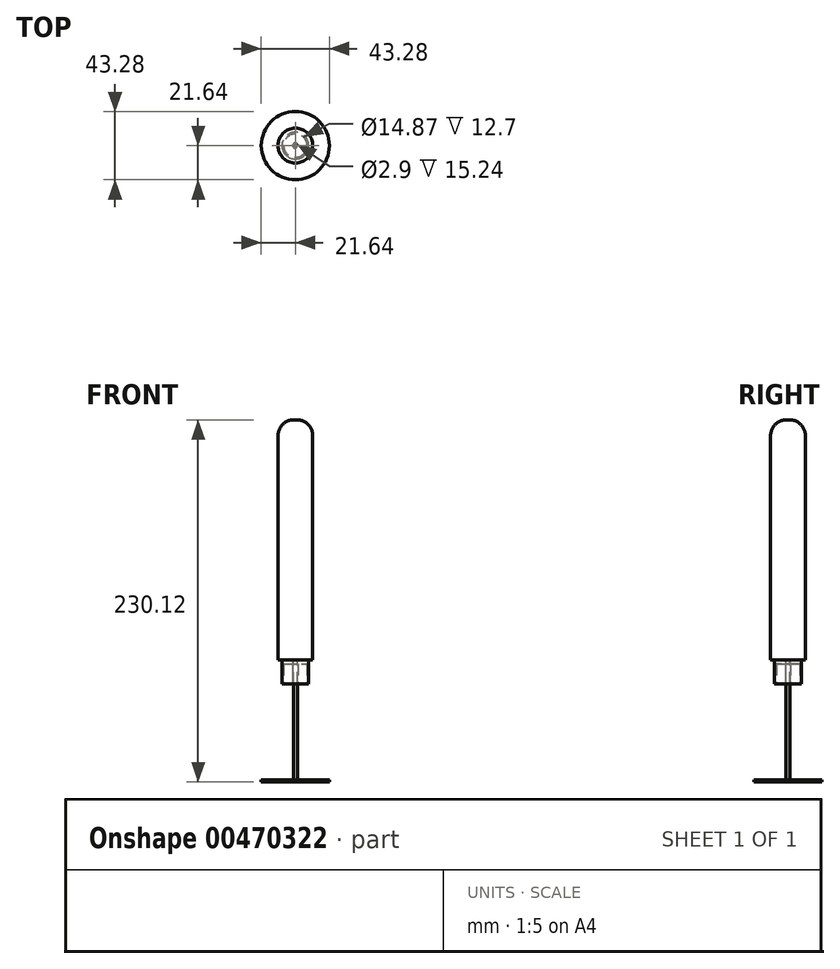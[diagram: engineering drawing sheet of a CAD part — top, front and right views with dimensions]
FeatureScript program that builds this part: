
annotation { "Feature Type Name" : "Feature", "Feature Type Description" : "" }
export const myFeature = defineFeature(function(context is Context, id is Id, definition is map)
    precondition{}
    {
        {
            var Q0;
            Q0=qCreatedBy(makeId("Top.planeOp"),FACE);
            var sketch = newSketch(context, id + "F0", { "sketchPlane" : qUnion([Q0])});
            skCircle(sketch, "E0", {"center": v(0, 0) * mm, "radius": 11.05 * mm});
            skSolve(sketch);
        }
        {
            var Q0;
            Q0 = qSketchRegion(id + "F0", true);
            extrude(context, id + "F1", {"entities" : qUnion([Q0]), "depth" : 152.4 * mm});
        }
        {
            var Q0;
            Q0=makeQuery(id+"F1.opExtrude","CAP_EDGE",EDGE,{"disambiguationData":[OSD([sQuery(id+"F0.wireOp",EDGE,"E0")])],"isStart":false});
            fillet(context, id + "F2", {"entities" : qUnion([Q0]), "radius" : 10.16 * mm, "tangentPropagation" : true, "allowEdgeOverflow" : false});
        }
        {
            var Q0;
            Q0=makeQuery(id+"F1.opExtrude","CAP_FACE",FACE,{"disambiguationData":[OSD([sQuery(id+"F0.wireOp",EDGE,"E0")])],"isStart":true});
            var sketch = newSketch(context, id + "F3", { "sketchPlane" : qUnion([Q0])});
            skCircle(sketch, "E1", {"center": v(0, 0) * mm, "radius": 1.3 * mm});
            skSolve(sketch);
        }
        {
            var Q0;
            Q0 = qSketchRegion(id + "F3", true);
            extrude(context, id + "F4", {"entities" : qUnion([Q0]), "operationType" : NewBodyOperationType.ADD, "depth" : 76.2 * mm});
        }
        {
            var Q0;
            Q0=makeQuery(id+"F1.opExtrude","CAP_FACE",FACE,{"disambiguationData":[OSD([sQuery(id+"F0.wireOp",EDGE,"E0")])],"isStart":true});
            var sketch = newSketch(context, id + "F5", { "sketchPlane" : qUnion([Q0])});
            skCircle(sketch, "E2", {"center": v(0, 0) * mm, "radius": 1.45 * mm});
            skCircle(sketch, "E3", {"center": v(0, 0) * mm, "radius": 8.5 * mm});
            skSolve(sketch);
        }
        {
            var Q0;
            Q0=makeQuery(id+"F5.imprint","IMPRINT",FACE,{"disambiguationData":[TD([[makeQuery(id+"F5.imprint","IMPRINT",EDGE,{"derivedFrom":sQuery(id+"F5.wireOp",EDGE,"E2")}),-1.0]])]});
            extrude(context, id + "F6", {"entities" : qUnion([Q0]), "operationType" : NewBodyOperationType.ADD, "depth" : 15.24 * mm});
        }
        {
            var Q0;
            Q0=makeQuery(id+"F6.opExtrude","CAP_FACE",FACE,{"disambiguationData":[OSD([sQuery(id+"F5.wireOp",EDGE,"E2"),sQuery(id+"F5.wireOp",EDGE,"E3")])],"isStart":false});
            var sketch = newSketch(context, id + "F7", { "sketchPlane" : qUnion([Q0])});
            skCircle(sketch, "E4", {"center": v(0, 0) * mm, "radius": 1.67 * mm});
            skCircle(sketch, "E5", {"center": v(0, 0) * mm, "radius": 7.44 * mm});
            skSolve(sketch);
        }
        {
            var Q0;
            Q0 = qSketchRegion(id + "F7", true);
            extrude(context, id + "F8", {"entities" : qUnion([Q0]), "operationType" : NewBodyOperationType.REMOVE, "oppositeDirection" : true, "depth" : 12.7 * mm});
        }
        {
            var Q0;
            Q0=makeQuery(id+"F4.opExtrude","CAP_FACE",FACE,{"disambiguationData":[OSD([sQuery(id+"F3.wireOp",EDGE,"E1")])],"isStart":false});
            var sketch = newSketch(context, id + "F9", { "sketchPlane" : qUnion([Q0])});
            skCircle(sketch, "E6", {"center": v(0, 0) * mm, "radius": 21.64 * mm});
            skSolve(sketch);
        }
        {
            var Q0;
            Q0 = qSketchRegion(id + "F9", true);
            extrude(context, id + "F10", {"entities" : qUnion([Q0]), "operationType" : NewBodyOperationType.ADD, "depth" : 1.52 * mm});
        }
    });
